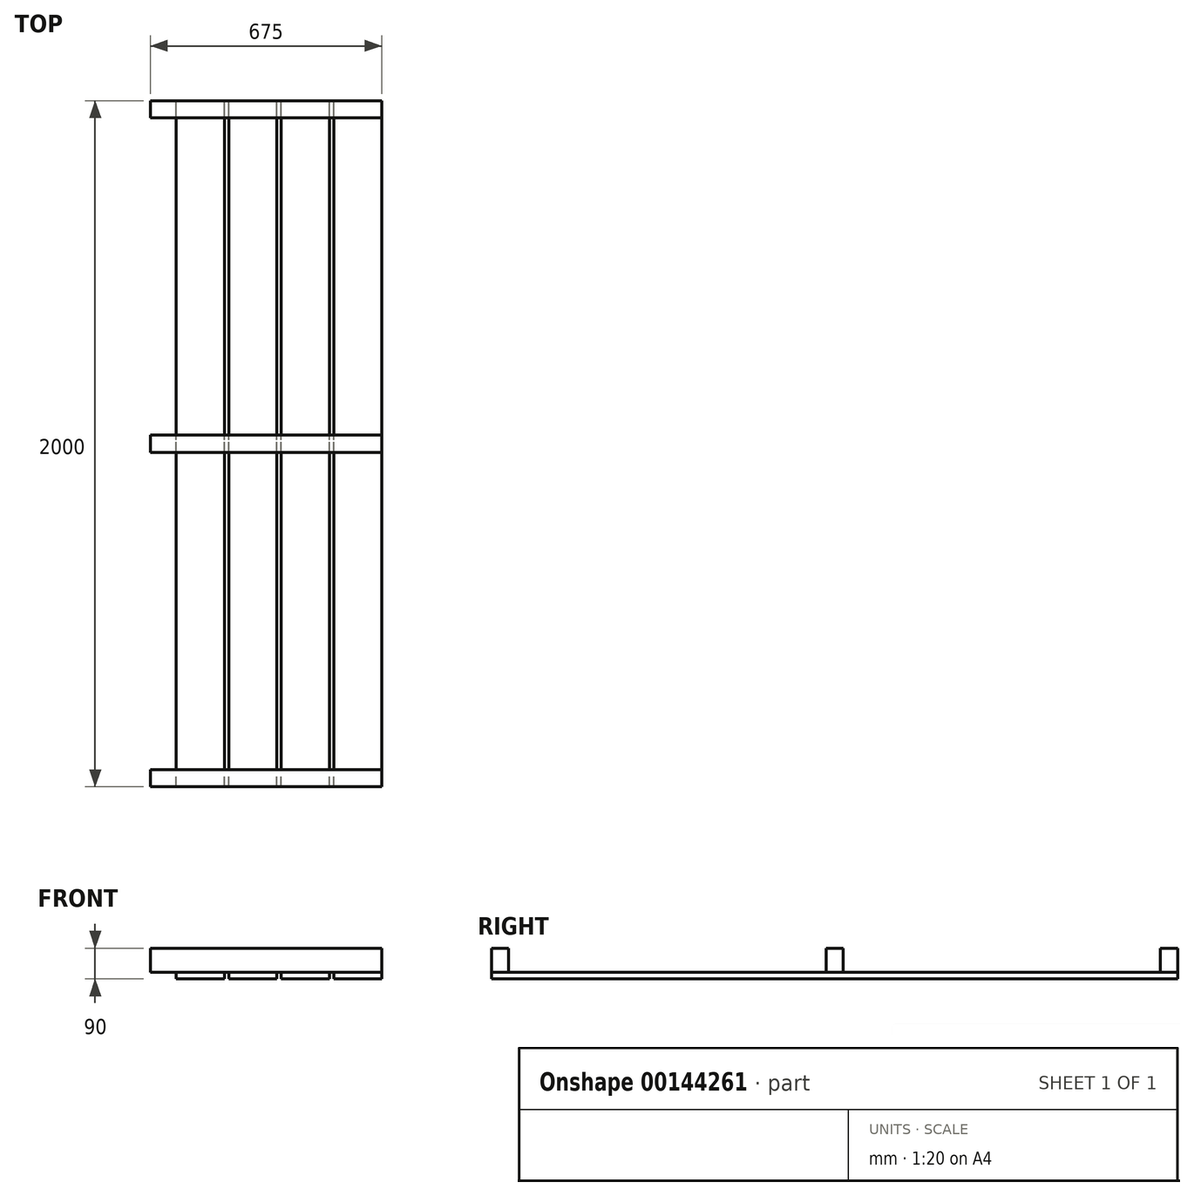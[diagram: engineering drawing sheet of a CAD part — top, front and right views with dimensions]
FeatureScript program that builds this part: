
annotation { "Feature Type Name" : "Feature", "Feature Type Description" : "" }
export const myFeature = defineFeature(function(context is Context, id is Id, definition is map)
    precondition{}
    {
        {
            var Q0;
            Q0=qCreatedBy(makeId("Front.planeOp"),FACE);
            var sketch = newSketch(context, id + "F0", { "sketchPlane" : qUnion([Q0])});
            skLineSegment(sketch, "E0.bottom", {"start": v(0, 0) * mm, "end": v(140, 0) * mm});
            skLineSegment(sketch, "E0.top", {"start": v(0, 20) * mm, "end": v(140, 20) * mm});
            skLineSegment(sketch, "E0.left", {"start": v(0, 0) * mm, "end": v(0, 20) * mm});
            skLineSegment(sketch, "E0.right", {"start": v(140, 0) * mm, "end": v(140, 20) * mm});
            skLineSegment(sketch, "E1.bottom", {"start": v(153, 0) * mm, "end": v(293, 0) * mm});
            skLineSegment(sketch, "E1.top", {"start": v(153, 20) * mm, "end": v(293, 20) * mm});
            skLineSegment(sketch, "E1.left", {"start": v(153, 0) * mm, "end": v(153, 20) * mm});
            skLineSegment(sketch, "E1.right", {"start": v(293, 0) * mm, "end": v(293, 20) * mm});
            skLineSegment(sketch, "E2.bottom", {"start": v(306, 0) * mm, "end": v(446, 0) * mm});
            skLineSegment(sketch, "E2.top", {"start": v(306, 20) * mm, "end": v(446, 20) * mm});
            skLineSegment(sketch, "E2.left", {"start": v(306, 0) * mm, "end": v(306, 20) * mm});
            skLineSegment(sketch, "E2.right", {"start": v(446, 0) * mm, "end": v(446, 20) * mm});
            skLineSegment(sketch, "E3.bottom", {"start": v(459, 0) * mm, "end": v(599, 0) * mm});
            skLineSegment(sketch, "E3.top", {"start": v(459, 20) * mm, "end": v(599, 20) * mm});
            skLineSegment(sketch, "E3.left", {"start": v(459, 0) * mm, "end": v(459, 20) * mm});
            skLineSegment(sketch, "E3.right", {"start": v(599, 0) * mm, "end": v(599, 20) * mm});
            skLineSegment(sketch, "E4.bottom", {"start": v(-13, 0) * mm, "end": v(-153, 0) * mm});
            skLineSegment(sketch, "E4.top", {"start": v(-13, 20) * mm, "end": v(-153, 20) * mm});
            skLineSegment(sketch, "E4.left", {"start": v(-13, 0) * mm, "end": v(-13, 20) * mm});
            skLineSegment(sketch, "E4.right", {"start": v(-153, 0) * mm, "end": v(-153, 20) * mm});
            skSolve(sketch);
        }
        {
            var Q0;
            Q0=makeQuery(id+"F0.imprint","IMPRINT",FACE,{"disambiguationData":[TD([[makeQuery(id+"F0.imprint","IMPRINT",EDGE,{"derivedFrom":sQuery(id+"F0.wireOp",EDGE,"E0.bottom")}),1.0]])]});
            var Q1;
            Q1=makeQuery(id+"F0.imprint","IMPRINT",FACE,{"disambiguationData":[TD([[makeQuery(id+"F0.imprint","IMPRINT",EDGE,{"derivedFrom":sQuery(id+"F0.wireOp",EDGE,"E1.bottom")}),1.0]])]});
            var Q2;
            Q2=makeQuery(id+"F0.imprint","IMPRINT",FACE,{"disambiguationData":[TD([[makeQuery(id+"F0.imprint","IMPRINT",EDGE,{"derivedFrom":sQuery(id+"F0.wireOp",EDGE,"E2.bottom")}),1.0]])]});
            var Q3;
            Q3=makeQuery(id+"F0.imprint","IMPRINT",FACE,{"disambiguationData":[TD([[makeQuery(id+"F0.imprint","IMPRINT",EDGE,{"derivedFrom":sQuery(id+"F0.wireOp",EDGE,"E4.bottom")}),-1.0]])]});
            extrude(context, id + "F1", {"entities" : qUnion([Q0, Q1, Q2, Q3]), "depth" : 2000 * mm});
        }
        {
            var Q0;
            Q0=makeQuery(id+"F1.opExtrude","SWEPT_FACE",FACE,{"disambiguationData":[OSD([sQuery(id+"F0.wireOp",EDGE,"E2.right")])]});
            var sketch = newSketch(context, id + "F2", { "sketchPlane" : qUnion([Q0])});
            skLineSegment(sketch, "E5.bottom", {"start": v(-2000, 20) * mm, "end": v(-1950, 20) * mm});
            skLineSegment(sketch, "E5.top", {"start": v(-2000, 90) * mm, "end": v(-1950, 90) * mm});
            skLineSegment(sketch, "E5.left", {"start": v(-2000, 20) * mm, "end": v(-2000, 90) * mm});
            skLineSegment(sketch, "E5.right", {"start": v(-1950, 20) * mm, "end": v(-1950, 90) * mm});
            skLineSegment(sketch, "E6.bottom", {"start": v(0, 20) * mm, "end": v(-50, 20) * mm});
            skLineSegment(sketch, "E6.top", {"start": v(0, 90) * mm, "end": v(-50, 90) * mm});
            skLineSegment(sketch, "E6.left", {"start": v(0, 20) * mm, "end": v(0, 90) * mm});
            skLineSegment(sketch, "E6.right", {"start": v(-50, 20) * mm, "end": v(-50, 90) * mm});
            skSolve(sketch);
        }
        {
            var Q0;
            Q0=makeQuery(id+"F2.imprint","IMPRINT",FACE,{"disambiguationData":[TD([[makeQuery(id+"F2.imprint","IMPRINT",EDGE,{"derivedFrom":sQuery(id+"F2.wireOp",EDGE,"E5.bottom")}),1.0]])]});
            var sketch = newSketch(context, id + "F3", { "sketchPlane" : qUnion([Q0])});
            skLineSegment(sketch, "E7.bottom", {"start": v(-1025, 20) * mm, "end": v(-975, 20) * mm});
            skLineSegment(sketch, "E7.top", {"start": v(-1025, 90) * mm, "end": v(-975, 90) * mm});
            skLineSegment(sketch, "E7.left", {"start": v(-1025, 20) * mm, "end": v(-1025, 90) * mm});
            skLineSegment(sketch, "E7.right", {"start": v(-975, 20) * mm, "end": v(-975, 90) * mm});
            skSolve(sketch);
        }
        {
            var Q0;
            Q0=qSketchRegion(id+"F2",true);
            var Q1;
            Q1=qSketchRegion(id+"F3",true);
            extrude(context, id + "F4", {"entities" : qUnion([Q0, Q1]), "oppositeDirection" : true, "depth" : 675 * mm});
        }
    });
